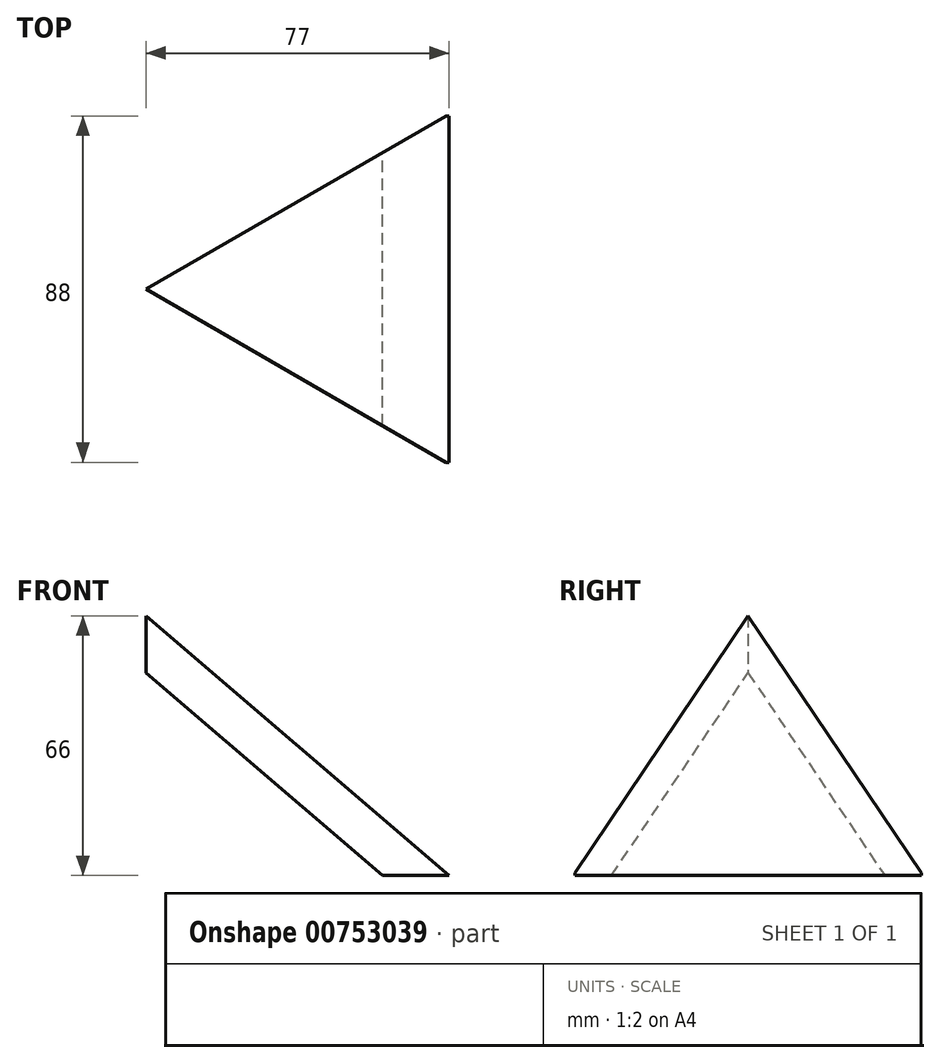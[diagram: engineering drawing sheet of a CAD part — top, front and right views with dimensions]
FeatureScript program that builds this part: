
annotation { "Feature Type Name" : "Feature", "Feature Type Description" : "" }
export const myFeature = defineFeature(function(context is Context, id is Id, definition is map)
    precondition{}
    {
        {
            var Q0;
            Q0=qCreatedBy(makeId("Front.planeOp"),FACE);
            var sketch = newSketch(context, id + "F0", { "sketchPlane" : qUnion([Q0])});
            skLineSegment(sketch, "E0", {"start": v(0, 0) * mm, "end": v(0, 66) * mm, "construction": true});
            skLineSegment(sketch, "E1", {"start": v(0, 0) * mm, "end": v(77, 0) * mm, "construction": true});
            skLineSegment(sketch, "E2", {"start": v(0, 66) * mm, "end": v(77, 0) * mm});
            skLineSegment(sketch, "E3", {"start": v(0, 66) * mm, "end": v(0, 51.51) * mm});
            skLineSegment(sketch, "E4", {"start": v(0, 51.51) * mm, "end": v(60.1, 0) * mm});
            skLineSegment(sketch, "E5", {"start": v(60.1, 0) * mm, "end": v(77, 0) * mm});
            skSolve(sketch);
        }
        {
            var Q0;
            Q0 = qSketchRegion(id + "F0", true);
            extrude(context, id + "F1", {"entities" : qUnion([Q0]), "endBound" : BoundingType.SYMMETRIC, "depth" : 66 * mm, "offsetDistance" : 25 * mm});
        }
        {
            var Q0;
            Q0 = qSketchRegion(id + "F0", true);
            extrude(context, id + "F2", {"entities" : qUnion([Q0]), "operationType" : NewBodyOperationType.ADD, "endBound" : BoundingType.SYMMETRIC, "depth" : 88 * mm, "offsetDistance" : 25 * mm});
        }
        {
            var Q0;
            Q0=qCreatedBy(makeId("Top.planeOp"),FACE);
            var sketch = newSketch(context, id + "F3", { "sketchPlane" : qUnion([Q0])});
            skCircle(sketch, "E6.cCircle", {"center": v(0, 0) * mm, "radius": 88.68 * mm, "construction": true});
            skLineSegment(sketch, "E6.0", {"start": v(88.68, 51.2) * mm, "end": v(88.68, -51.2) * mm});
            skLineSegment(sketch, "E6.1", {"start": v(88.68, -51.2) * mm, "end": v(0, -102.4) * mm});
            skLineSegment(sketch, "E6.2", {"start": v(0, -102.4) * mm, "end": v(-88.68, -51.2) * mm});
            skLineSegment(sketch, "E6.3", {"start": v(-88.68, -51.2) * mm, "end": v(-88.68, 51.2) * mm});
            skLineSegment(sketch, "E6.4", {"start": v(-88.68, 51.2) * mm, "end": v(0, 102.4) * mm});
            skLineSegment(sketch, "E6.5", {"start": v(0, 102.4) * mm, "end": v(88.68, 51.2) * mm});
            skPoint(sketch, "E6.0.midPoint", {"position": v(88.68, 0) * mm});
            skLineSegment(sketch, "E7", {"start": v(0, 0) * mm, "end": v(88.68, -51.2) * mm});
            skLineSegment(sketch, "E8", {"start": v(88.68, 51.2) * mm, "end": v(0, 0) * mm});
            skSolve(sketch);
        }
        {
            var Q0;
            Q0=makeQuery(id+"F3.imprint","IMPRINT",FACE,{"disambiguationData":[TD([[makeQuery(id+"F3.imprint","IMPRINT",EDGE,{"derivedFrom":sQuery(id+"F3.wireOp",EDGE,"E6.0")}),-1.0]])]});
            extrude(context, id + "F4", {"entities" : qUnion([Q0]), "operationType" : NewBodyOperationType.INTERSECT, "endBound" : BoundingType.THROUGH_ALL, "depth" : 25 * mm, "offsetDistance" : 25 * mm});
        }
    });
